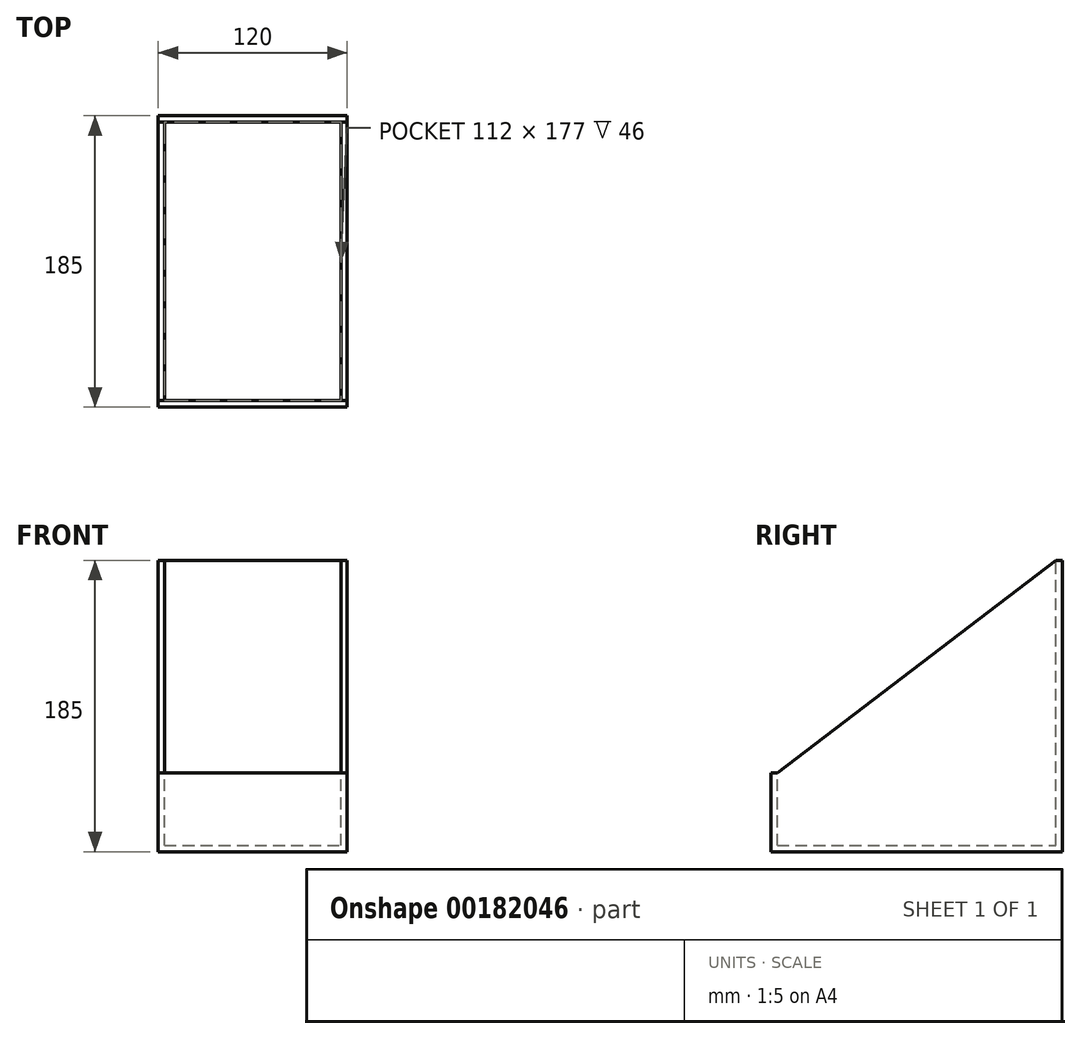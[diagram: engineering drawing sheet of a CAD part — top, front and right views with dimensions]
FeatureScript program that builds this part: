
annotation { "Feature Type Name" : "Feature", "Feature Type Description" : "" }
export const myFeature = defineFeature(function(context is Context, id is Id, definition is map)
    precondition{}
    {
        {
            var Q0;
            Q0=qCreatedBy(makeId("Front.planeOp"),FACE);
            var sketch = newSketch(context, id + "F0", { "sketchPlane" : qUnion([Q0])});
            skLineSegment(sketch, "E0.bottom", {"start": v(0, 0) * mm, "end": v(-120, 0) * mm});
            skLineSegment(sketch, "E0.top", {"start": v(0, -185) * mm, "end": v(-120, -185) * mm});
            skLineSegment(sketch, "E0.left", {"start": v(0, 0) * mm, "end": v(0, -185) * mm});
            skLineSegment(sketch, "E0.right", {"start": v(-120, 0) * mm, "end": v(-120, -185) * mm});
            skSolve(sketch);
        }
        {
            var Q0;
            Q0 = qSketchRegion(id + "F0", true);
            extrude(context, id + "F1", {"entities" : qUnion([Q0]), "oppositeDirection" : true, "depth" : 185 * mm});
        }
        {
            var Q0;
            Q0=makeQuery(id+"F1.opExtrude","SWEPT_FACE",FACE,{"disambiguationData":[OSD([sQuery(id+"F0.wireOp",EDGE,"E0.left")])]});
            var sketch = newSketch(context, id + "F2", { "sketchPlane" : qUnion([Q0])});
            skLineSegment(sketch, "E1.0", {"start": v(185, 0) * mm, "end": v(0, 0) * mm, "construction": true});
            skLineSegment(sketch, "E2", {"start": v(181, 0) * mm, "end": v(4, -135) * mm});
            skLineSegment(sketch, "E3", {"start": v(4, -135) * mm, "end": v(0, -135) * mm});
            skLineSegment(sketch, "E4", {"start": v(0, -135) * mm, "end": v(0, 0) * mm});
            skLineSegment(sketch, "E5", {"start": v(181, 0) * mm, "end": v(0, 0) * mm});
            skSolve(sketch);
        }
        {
            var Q0;
            Q0 = qSketchRegion(id + "F2", true);
            extrude(context, id + "F3", {"entities" : qUnion([Q0]), "operationType" : NewBodyOperationType.REMOVE, "endBound" : BoundingType.UP_TO_NEXT, "oppositeDirection" : true, "depth" : 25 * mm});
        }
        {
            var Q0;
            Q0=qCreatedBy(makeId("Top.planeOp"),FACE);
            var sketch = newSketch(context, id + "F4", { "sketchPlane" : qUnion([Q0])});
            skLineSegment(sketch, "E6.0", {"start": v(-120, 181) * mm, "end": v(-120, 4) * mm, "construction": true});
            skLineSegment(sketch, "E6.1", {"start": v(0, 181) * mm, "end": v(0, 4) * mm, "construction": true});
            skLineSegment(sketch, "E7.0", {"start": v(-116, 366) * mm, "end": v(-116, 4) * mm, "construction": true});
            skLineSegment(sketch, "E8.0", {"start": v(-4, 181) * mm, "end": v(-4, 4) * mm, "construction": true});
            skLineSegment(sketch, "E9.bottom", {"start": v(-116, 4) * mm, "end": v(-4, 4) * mm});
            skLineSegment(sketch, "E9.top", {"start": v(-116, 181) * mm, "end": v(-4, 181) * mm});
            skLineSegment(sketch, "E9.left", {"start": v(-116, 4) * mm, "end": v(-116, 181) * mm});
            skLineSegment(sketch, "E9.right", {"start": v(-4, 4) * mm, "end": v(-4, 181) * mm});
            skSolve(sketch);
        }
        {
            var Q0;
            Q0 = qSketchRegion(id + "F4", true);
            extrude(context, id + "F5", {"entities" : qUnion([Q0]), "operationType" : NewBodyOperationType.REMOVE, "oppositeDirection" : true, "depth" : 181 * mm});
        }
    });
